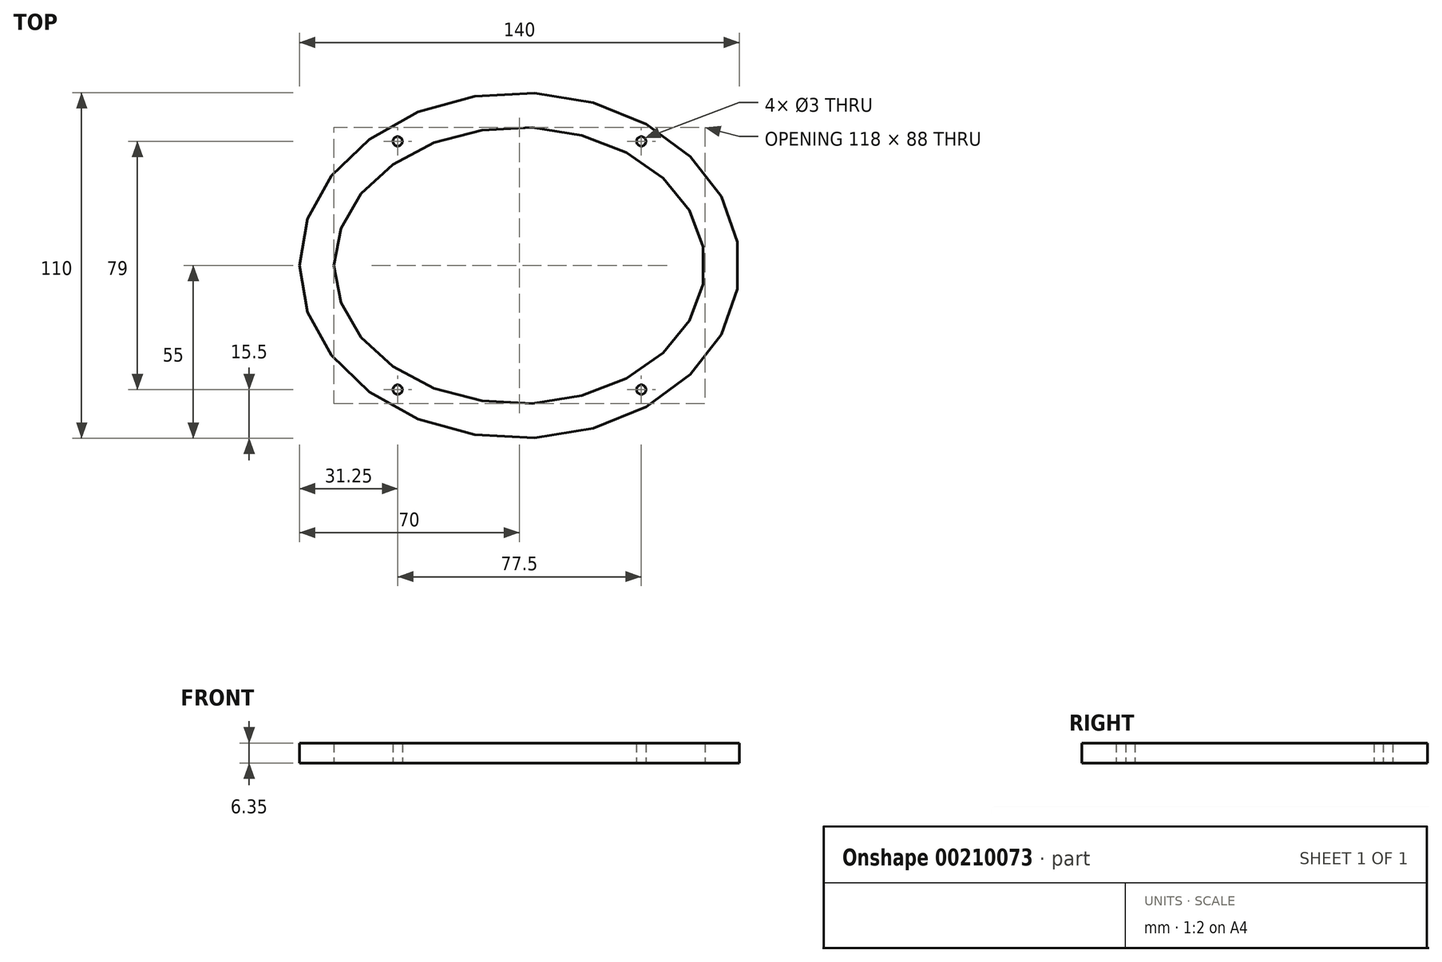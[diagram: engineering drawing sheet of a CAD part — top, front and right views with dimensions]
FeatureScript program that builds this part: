
annotation { "Feature Type Name" : "Feature", "Feature Type Description" : "" }
export const myFeature = defineFeature(function(context is Context, id is Id, definition is map)
    precondition{}
    {
        {
            var Q0;
            Q0=qCreatedBy(makeId("Top.planeOp"),FACE);
            var sketch = newSketch(context, id + "F0", { "sketchPlane" : qUnion([Q0])});
            skEllipse(sketch, "E0", {"center": v(0, 0) * mm, "majorRadius": 70 * mm, "minorRadius": 55 * mm, "majorAxis": v(-1, 0)});
            skLineSegment(sketch, "E1", {"start": v(0, 55) * mm, "end": v(0, -55) * mm, "construction": true});
            skLineSegment(sketch, "E2", {"start": v(-70, 0) * mm, "end": v(70, 0) * mm, "construction": true});
            skPoint(sketch, "E3", {"position": v(38.75, 39.5) * mm});
            skPoint(sketch, "E4", {"position": v(38.75, -39.5) * mm});
            skPoint(sketch, "E5", {"position": v(-38.75, -39.5) * mm});
            skPoint(sketch, "E6", {"position": v(-38.75, 39.5) * mm});
            skCircle(sketch, "E7", {"center": v(-38.75, 39.5) * mm, "radius": 1.5 * mm});
            skCircle(sketch, "E8", {"center": v(38.75, 39.5) * mm, "radius": 1.5 * mm});
            skCircle(sketch, "E9", {"center": v(38.75, -39.5) * mm, "radius": 1.5 * mm});
            skCircle(sketch, "E10", {"center": v(-38.75, -39.5) * mm, "radius": 1.5 * mm});
            skEllipse(sketch, "E11", {"center": v(0, 0) * mm, "majorRadius": 59 * mm, "minorRadius": 44 * mm, "majorAxis": v(-1, 0)});
            skSolve(sketch);
        }
        {
            var Q0;
            Q0=qSketchRegion(id+"F0",true);
            extrude(context, id + "F1", {"entities" : qUnion([Q0]), "depth" : 6.35 * mm});
        }
    });
